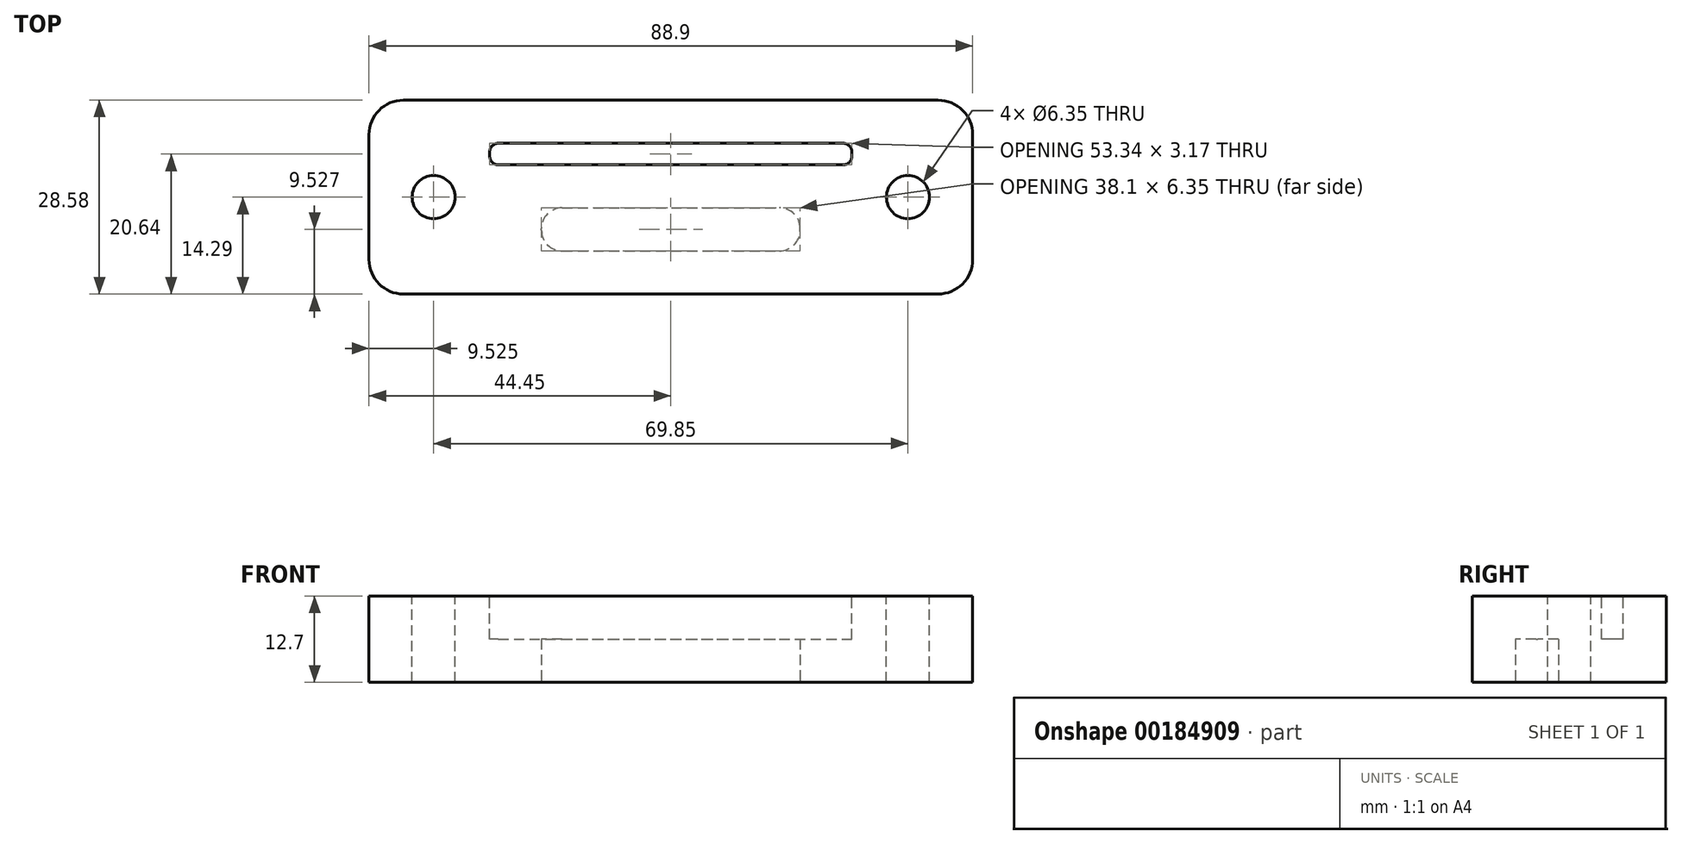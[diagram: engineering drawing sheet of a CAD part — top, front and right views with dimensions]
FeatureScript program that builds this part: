
annotation { "Feature Type Name" : "Feature", "Feature Type Description" : "" }
export const myFeature = defineFeature(function(context is Context, id is Id, definition is map)
    precondition{}
    {
        {
            var Q0;
            Q0=qCreatedBy(makeId("Top.planeOp"),FACE);
            var sketch = newSketch(context, id + "F0", { "sketchPlane" : qUnion([Q0])});
            skLineSegment(sketch, "E0.bottom", {"start": v(-44.45, 14.29) * mm, "end": v(44.45, 14.29) * mm});
            skLineSegment(sketch, "E0.top", {"start": v(-44.45, -14.29) * mm, "end": v(44.45, -14.29) * mm});
            skLineSegment(sketch, "E0.left", {"start": v(-44.45, 14.29) * mm, "end": v(-44.45, -14.29) * mm});
            skLineSegment(sketch, "E0.right", {"start": v(44.45, 14.29) * mm, "end": v(44.45, -14.29) * mm});
            skPoint(sketch, "E0.middle", {"position": v(0, 0) * mm});
            skSolve(sketch);
        }
        {
            var Q0;
            Q0=makeQuery(id+"F0.imprint","IMPRINT",FACE,{"disambiguationData":[TD([[makeQuery(id+"F0.imprint","IMPRINT",EDGE,{"derivedFrom":sQuery(id+"F0.wireOp",EDGE,"E0.bottom")}),-1.0]])]});
            extrude(context, id + "F1", {"entities" : qUnion([Q0]), "depth" : 12.7 * mm});
        }
        {
            var Q0;
            Q0=makeQuery(id+"F1.opExtrude","CAP_FACE",FACE,{"disambiguationData":[OSD([sQuery(id+"F0.wireOp",EDGE,"E0.bottom"),sQuery(id+"F0.wireOp",EDGE,"E0.top"),sQuery(id+"F0.wireOp",EDGE,"E0.left"),sQuery(id+"F0.wireOp",EDGE,"E0.right")])],"isStart":false});
            var sketch = newSketch(context, id + "F2", { "sketchPlane" : qUnion([Q0])});
            skLineSegment(sketch, "E1.bottom", {"start": v(-25.4, 7.94) * mm, "end": v(25.4, 7.94) * mm});
            skLineSegment(sketch, "E1.top", {"start": v(-25.4, 4.76) * mm, "end": v(25.4, 4.76) * mm});
            skLineSegment(sketch, "E1.left", {"start": v(-26.67, 6.67) * mm, "end": v(-26.67, 6.03) * mm});
            skLineSegment(sketch, "E1.right", {"start": v(26.67, 6.67) * mm, "end": v(26.67, 6.03) * mm});
            skPoint(sketch, "E2.visualSharp", {"position": v(-26.67, 7.94) * mm});
            skArc(sketch, "E2.filletArc", {"start": v(-25.4, 7.94) * mm, "mid": v(-26.3, 7.57) * mm, "end": v(-26.67, 6.67) * mm});
            skPoint(sketch, "E3.visualSharp", {"position": v(-26.67, 4.76) * mm});
            skArc(sketch, "E3.filletArc", {"start": v(-26.67, 6.03) * mm, "mid": v(-26.3, 5.13) * mm, "end": v(-25.4, 4.76) * mm});
            skPoint(sketch, "E4.visualSharp", {"position": v(26.67, 7.94) * mm});
            skArc(sketch, "E4.filletArc", {"start": v(26.67, 6.67) * mm, "mid": v(26.3, 7.57) * mm, "end": v(25.4, 7.94) * mm});
            skPoint(sketch, "E5.visualSharp", {"position": v(26.67, 4.76) * mm});
            skArc(sketch, "E5.filletArc", {"start": v(25.4, 4.76) * mm, "mid": v(26.3, 5.13) * mm, "end": v(26.67, 6.03) * mm});
            skSolve(sketch);
        }
        {
            var Q0;
            Q0=makeQuery(id+"F2.imprint","IMPRINT",FACE,{"disambiguationData":[TD([[makeQuery(id+"F2.imprint","IMPRINT",EDGE,{"derivedFrom":sQuery(id+"F2.wireOp",EDGE,"E1.bottom")}),-1.0]])]});
            extrude(context, id + "F3", {"entities" : qUnion([Q0]), "operationType" : NewBodyOperationType.REMOVE, "oppositeDirection" : true, "depth" : 6.35 * mm});
        }
        {
            var Q0;
            Q0=makeQuery(id+"F1.opExtrude","SWEPT_EDGE",EDGE,{"disambiguationData":[OSD([sQuery(id+"F0.wireOp",EDGE,"E0.top"),sQuery(id+"F0.wireOp",EDGE,"E0.right")])]});
            var Q1;
            Q1=makeQuery(id+"F1.opExtrude","SWEPT_EDGE",EDGE,{"disambiguationData":[OSD([sQuery(id+"F0.wireOp",EDGE,"E0.bottom"),sQuery(id+"F0.wireOp",EDGE,"E0.right")])]});
            var Q2;
            Q2=makeQuery(id+"F1.opExtrude","SWEPT_EDGE",EDGE,{"disambiguationData":[OSD([sQuery(id+"F0.wireOp",EDGE,"E0.top"),sQuery(id+"F0.wireOp",EDGE,"E0.left")])]});
            var Q3;
            Q3=makeQuery(id+"F1.opExtrude","SWEPT_EDGE",EDGE,{"disambiguationData":[OSD([sQuery(id+"F0.wireOp",EDGE,"E0.bottom"),sQuery(id+"F0.wireOp",EDGE,"E0.left")])]});
            fillet(context, id + "F4", {"entities" : qUnion([Q0, Q1, Q2, Q3]), "radius" : 5.08 * mm, "tangentPropagation" : true, "allowEdgeOverflow" : false});
        }
        {
            var Q0;
            Q0=makeQuery(id+"F1.opExtrude","CAP_FACE",FACE,{"disambiguationData":[OSD([sQuery(id+"F0.wireOp",EDGE,"E0.bottom"),sQuery(id+"F0.wireOp",EDGE,"E0.top"),sQuery(id+"F0.wireOp",EDGE,"E0.left"),sQuery(id+"F0.wireOp",EDGE,"E0.right")])],"isStart":true});
            var sketch = newSketch(context, id + "F5", { "sketchPlane" : qUnion([Q0])});
            skLineSegment(sketch, "E6.bottom", {"start": v(-16, 7.94) * mm, "end": v(16, 7.94) * mm});
            skLineSegment(sketch, "E6.top", {"start": v(-16, 1.59) * mm, "end": v(16, 1.59) * mm});
            skLineSegment(sketch, "E6.left", {"start": v(-19.05, 4.89) * mm, "end": v(-19.05, 4.64) * mm});
            skLineSegment(sketch, "E6.right", {"start": v(19.05, 4.89) * mm, "end": v(19.05, 4.64) * mm});
            skPoint(sketch, "E7.visualSharp", {"position": v(19.05, 7.94) * mm});
            skArc(sketch, "E7.filletArc", {"start": v(19.05, 4.89) * mm, "mid": v(18.16, 7.04) * mm, "end": v(16, 7.94) * mm});
            skPoint(sketch, "E8.visualSharp", {"position": v(19.05, 1.59) * mm});
            skArc(sketch, "E8.filletArc", {"start": v(16, 1.59) * mm, "mid": v(18.16, 2.48) * mm, "end": v(19.05, 4.64) * mm});
            skPoint(sketch, "E9.visualSharp", {"position": v(-19.05, 1.59) * mm});
            skArc(sketch, "E9.filletArc", {"start": v(-19.05, 4.64) * mm, "mid": v(-18.16, 2.48) * mm, "end": v(-16, 1.59) * mm});
            skPoint(sketch, "E10.visualSharp", {"position": v(-19.05, 7.94) * mm});
            skArc(sketch, "E10.filletArc", {"start": v(-16, 7.94) * mm, "mid": v(-18.16, 7.04) * mm, "end": v(-19.05, 4.89) * mm});
            skSolve(sketch);
        }
        {
            var Q0;
            Q0=makeQuery(id+"F5.imprint","IMPRINT",FACE,{"disambiguationData":[TD([[makeQuery(id+"F5.imprint","IMPRINT",EDGE,{"derivedFrom":sQuery(id+"F5.wireOp",EDGE,"E6.bottom")}),-1.0]])]});
            extrude(context, id + "F6", {"entities" : qUnion([Q0]), "operationType" : NewBodyOperationType.REMOVE, "oppositeDirection" : true, "depth" : 6.35 * mm});
        }
        {
            var Q0;
            Q0=makeQuery(id+"F1.opExtrude","CAP_FACE",FACE,{"disambiguationData":[OSD([sQuery(id+"F0.wireOp",EDGE,"E0.bottom"),sQuery(id+"F0.wireOp",EDGE,"E0.top"),sQuery(id+"F0.wireOp",EDGE,"E0.left"),sQuery(id+"F0.wireOp",EDGE,"E0.right")])],"isStart":false});
            var sketch = newSketch(context, id + "F7", { "sketchPlane" : qUnion([Q0])});
            skCircle(sketch, "E11", {"center": v(-34.93, 0) * mm, "radius": 3.18 * mm});
            skPoint(sketch, "E11.centerSnap0", {"position": v(-44.45, 0) * mm});
            skCircle(sketch, "E12", {"center": v(34.93, 0) * mm, "radius": 3.18 * mm});
            skPoint(sketch, "E12.centerSnap0", {"position": v(44.45, 0) * mm});
            skSolve(sketch);
        }
        {
            var Q0;
            Q0 = qSketchRegion(id + "F7", true);
            extrude(context, id + "F8", {"entities" : qUnion([Q0]), "operationType" : NewBodyOperationType.REMOVE, "oppositeDirection" : true, "depth" : 25.4 * mm});
        }
    });
